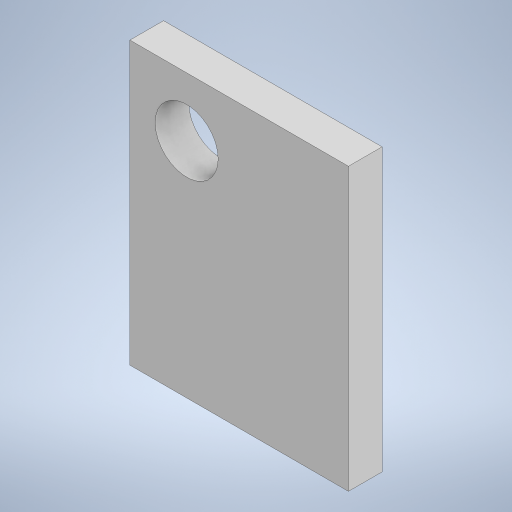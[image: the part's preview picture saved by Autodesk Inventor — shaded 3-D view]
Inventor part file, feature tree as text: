
AUTODESK INVENTOR PART (.ipt)
format: ipt  version: 2023 (Build 270158000, 158)  size: 207,872 bytes
history: native  units: in
note: dims shown in document units (in); Inventor stores cm internally (conversion verified against a paired STEP export)
features: sketch x2, extrude x1, hole x1
ambient origin geometry x8: Origin, YZ Plane, XZ Plane, XY Plane, X Axis, Y Axis, Z Axis, Center Point
bodies: Solid1 (feature_tree)
feature tree (4):
  extrude  "Extrusion1"  Depth=0.5276in
  hole  "Hole1"  [1 undecoded]
  sketch  "Sketch1"  dims[d0=0.4094in d1=0.5276in]
  sketch  "Sketch2"  dims[d2=0.063in d3=0.0in d4=0.1102in d5=0.1063in d6=0.1181in d7=0.2362in d8=0.1575in d9=0.0787in d10=90.0deg d11=0.315in d12=0.0in]
note: 1 required parameter value undecoded (feature->parameter linkage not recoverable at this tier; creation-order binding heuristic only, values carry confidence <= 0.55)
